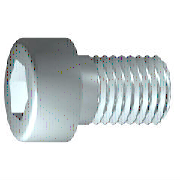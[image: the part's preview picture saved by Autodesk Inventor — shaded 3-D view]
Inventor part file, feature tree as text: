
AUTODESK INVENTOR PART (.ipt)
format: ipt  version: 2013 (Build 170138000, 138)  size: 179,200 bytes
history: native  units: mm (DEFAULTED — no unit token found)
features: sketch x2, extrude x1, plane x1
ambient origin geometry x7: Origin, YZ Plane, XY Plane, X Axis, Y Axis, Z Axis, Center Point
bodies: Solid1 (feature_tree), Body (feature_tree)
feature tree (4):
  extrude  "Slot"  Depth=0.276053mm
  plane  "Work Plane1"
  sketch  "Sketch1"  dims[d0=17.0mm d1=0.276053mm]
  sketch  "Sketch2"  dims[d2=2.5mm d3=1.25mm d4=60.0deg d5=2.5mm d6=2.5mm d7=2.309401mm d8=4.5mm d10=90.0deg d11=10.0mm d9=0.0mm d12=17.0mm d13=0.0mm d14=0.276052mm d15=0.276053mm d16=0.25mm d17=0.0mm d18=0.0mm d19=35.0mm d27=45.0deg d28=0.1mm d29=0.1mm]
